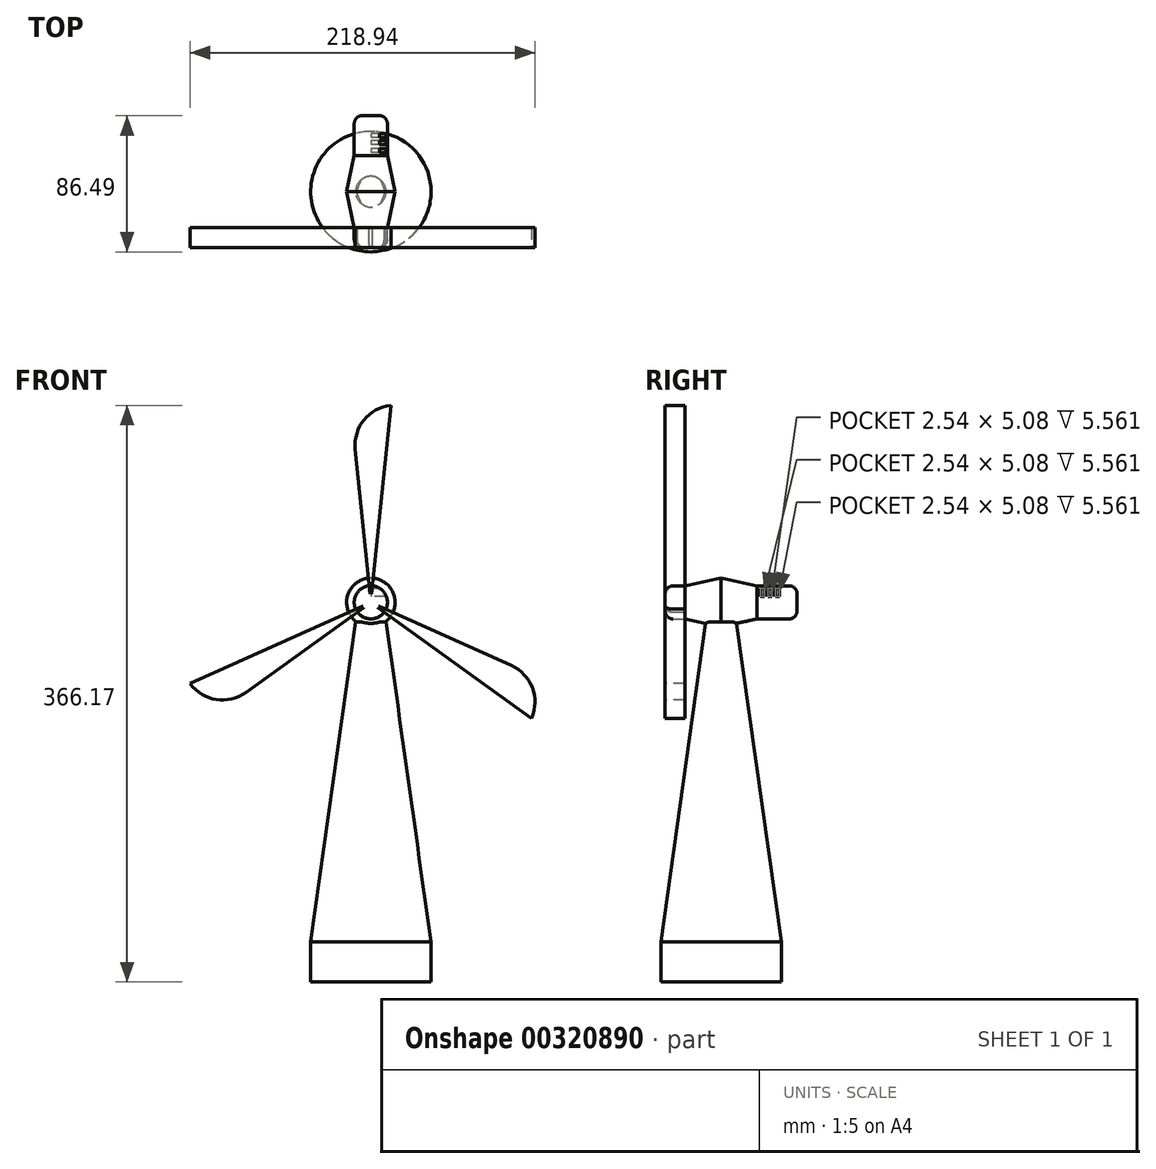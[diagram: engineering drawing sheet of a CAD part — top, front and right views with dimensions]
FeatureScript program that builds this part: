
annotation { "Feature Type Name" : "Feature", "Feature Type Description" : "" }
export const myFeature = defineFeature(function(context is Context, id is Id, definition is map)
    precondition{}
    {
        {
            var Q0;
            Q0=qCreatedBy(makeId("Top.planeOp"),FACE);
            var sketch = newSketch(context, id + "F0", { "sketchPlane" : qUnion([Q0])});
            skCircle(sketch, "E0", {"center": v(0, 0) * mm, "radius": 38.23 * mm});
            skSolve(sketch);
        }
        {
            var Q0;
            Q0=makeQuery(id+"F0.imprint","IMPRINT",FACE,{"disambiguationData":[TD([[makeQuery(id+"F0.imprint","IMPRINT",EDGE,{"derivedFrom":sQuery(id+"F0.wireOp",EDGE,"E0")}),1.0]])]});
            extrude(context, id + "F1", {"entities" : qUnion([Q0]), "depth" : 203.2 * mm, "hasDraft" : true, "draftAngle" : 8 * degree, "draftPullDirection" : true, "hasSecondDirection" : true, "secondDirectionOppositeDirection" : true, "secondDirectionDepth" : 25.4 * mm});
        }
        {
            var Q0;
            Q0=qCreatedBy(makeId("Front.planeOp"),FACE);
            var sketch = newSketch(context, id + "F2", { "sketchPlane" : qUnion([Q0])});
            skCircle(sketch, "E1", {"center": v(0, 215.62) * mm, "radius": 15.4 * mm});
            skSolve(sketch);
        }
        {
            var Q0;
            Q0=makeQuery(id+"F2.imprint","IMPRINT",FACE,{"disambiguationData":[TD([[makeQuery(id+"F2.imprint","IMPRINT",EDGE,{"derivedFrom":sQuery(id+"F2.wireOp",EDGE,"E1")}),1.0]])]});
            extrude(context, id + "F3", {"entities" : qUnion([Q0]), "operationType" : NewBodyOperationType.ADD, "depth" : 45.72 * mm, "hasDraft" : true, "draftAngle" : 12 * degree, "draftPullDirection" : true, "symmetric" : true});
        }
        {
            var Q0;
            Q0=makeQuery(id+"F3.opExtrude","CAP_FACE",FACE,{"disambiguationData":[OSD([sQuery(id+"F2.wireOp",EDGE,"E1")])],"isStart":false});
            var sketch = newSketch(context, id + "F4", { "sketchPlane" : qUnion([Q0])});
            skCircle(sketch, "E2", {"center": v(0, 215.62) * mm, "radius": 10.58 * mm});
            skSolve(sketch);
        }
        {
            var Q0;
            Q0=makeQuery(id+"F4.imprint","IMPRINT",FACE,{"disambiguationData":[TD([[makeQuery(id+"F4.imprint","IMPRINT",EDGE,{"derivedFrom":makeQuery(id+"F3.opExtrude","CAP_EDGE",EDGE,{"disambiguationData":[OSD([sQuery(id+"F2.wireOp",EDGE,"E1")])],"isStart":false})}),1.0]])]});
            extrude(context, id + "F5", {"entities" : qUnion([Q0]), "operationType" : NewBodyOperationType.ADD, "depth" : 6.35 * mm});
        }
        {
            var Q0;
            Q0=makeQuery(id+"F5.opExtrude","CAP_FACE",FACE,{"disambiguationData":[OSD([sQuery(id+"F2.wireOp",EDGE,"E1")])],"isStart":false});
            extrude(context, id + "F6", {"entities" : qUnion([Q0]), "operationType" : NewBodyOperationType.ADD, "depth" : 6.35 * mm});
        }
        {
            var Q0;
            Q0=makeQuery(id+"F6.opExtrude","CAP_FACE",FACE,{"disambiguationData":[OSD([sQuery(id+"F2.wireOp",EDGE,"E1")])],"isStart":false});
            fillet(context, id + "F7", {"entities" : qUnion([Q0]), "radius" : 5.08 * mm, "tangentPropagation" : true, "allowEdgeOverflow" : false});
        }
        {
            var Q0;
            Q0=makeQuery(id+"F6.opExtrude","CAP_FACE",FACE,{"disambiguationData":[OSD([sQuery(id+"F2.wireOp",EDGE,"E1")])],"isStart":false});
            var sketch = newSketch(context, id + "F8", { "sketchPlane" : qUnion([Q0])});
            skLineSegment(sketch, "E3", {"start": v(0, 340.77) * mm, "end": v(-12.7, 340.77) * mm});
            skLineSegment(sketch, "E4", {"start": v(0, 340.77) * mm, "end": v(12.7, 340.77) * mm});
            skLineSegment(sketch, "E5", {"start": v(-12.7, 340.77) * mm, "end": v(0, 215.62) * mm});
            skLineSegment(sketch, "E6", {"start": v(12.7, 340.77) * mm, "end": v(0, 215.62) * mm});
            skLineSegment(sketch, "E7.1.0", {"start": v(-108.38, 153.05) * mm, "end": v(-102.03, 142.05) * mm});
            skLineSegment(sketch, "E7.1.1", {"start": v(-108.38, 153.05) * mm, "end": v(-114.73, 164.05) * mm});
            skLineSegment(sketch, "E7.1.2", {"start": v(-102.03, 142.05) * mm, "end": v(0, 215.62) * mm});
            skLineSegment(sketch, "E7.1.3", {"start": v(-114.73, 164.05) * mm, "end": v(0, 215.62) * mm});
            skLineSegment(sketch, "E7.2.0", {"start": v(108.38, 153.05) * mm, "end": v(114.73, 164.05) * mm});
            skLineSegment(sketch, "E7.2.1", {"start": v(108.38, 153.05) * mm, "end": v(102.03, 142.05) * mm});
            skLineSegment(sketch, "E7.2.2", {"start": v(114.73, 164.05) * mm, "end": v(0, 215.62) * mm});
            skLineSegment(sketch, "E7.2.3", {"start": v(102.03, 142.05) * mm, "end": v(0, 215.62) * mm});
            skPoint(sketch, "E7.center", {"position": v(0, 215.62) * mm});
            skSolve(sketch);
        }
        {
            var Q0;
            {var subQ6=sQuery(id+"F8.wireOp",EDGE,"E3");Q0=makeQuery(id+"F8.imprint","IMPRINT",FACE,{"disambiguationData":[TD([[makeQuery(id+"F8.imprint","IMPRINT",EDGE,{"derivedFrom":subQ6}),1.0]])]});}
            var Q1;
            {var subQ6=sQuery(id+"F8.wireOp",EDGE,"E7.1.0");Q1=makeQuery(id+"F8.imprint","IMPRINT",FACE,{"disambiguationData":[TD([[makeQuery(id+"F8.imprint","IMPRINT",EDGE,{"derivedFrom":subQ6}),1.0]])]});}
            var Q2;
            {var subQ6=sQuery(id+"F8.wireOp",EDGE,"E7.2.0");Q2=makeQuery(id+"F8.imprint","IMPRINT",FACE,{"disambiguationData":[TD([[makeQuery(id+"F8.imprint","IMPRINT",EDGE,{"derivedFrom":subQ6}),1.0]])]});}
            extrude(context, id + "F9", {"entities" : qUnion([Q0, Q1, Q2]), "operationType" : NewBodyOperationType.ADD, "oppositeDirection" : true, "depth" : 12.7 * mm});
        }
        {
            var Q0;
            Q0=makeQuery(id+"F9.opExtrude","SWEPT_EDGE",EDGE,{"disambiguationData":[OSD([sQuery(id+"F8.wireOp",EDGE,"E3"),sQuery(id+"F8.wireOp",EDGE,"E5")])]});
            var Q1;
            Q1=makeQuery(id+"F9.opExtrude","SWEPT_EDGE",EDGE,{"disambiguationData":[OSD([sQuery(id+"F8.wireOp",EDGE,"E7.1.0"),sQuery(id+"F8.wireOp",EDGE,"E7.1.2")])]});
            var Q2;
            Q2=makeQuery(id+"F9.opExtrude","SWEPT_EDGE",EDGE,{"disambiguationData":[OSD([sQuery(id+"F8.wireOp",EDGE,"E7.2.0"),sQuery(id+"F8.wireOp",EDGE,"E7.2.2")])]});
            fillet(context, id + "F10", {"entities" : qUnion([Q0, Q1, Q2]), "radius" : 25.4 * mm, "tangentPropagation" : true, "allowEdgeOverflow" : false});
        }
        {
            var Q0;
            Q0=makeQuery(id+"F3.opExtrude","CAP_FACE",FACE,{"disambiguationData":[OSD([sQuery(id+"F2.wireOp",EDGE,"E1")])],"isStart":true});
            extrude(context, id + "F11", {"entities" : qUnion([Q0]), "operationType" : NewBodyOperationType.ADD, "depth" : 25.4 * mm});
        }
        {
            var Q0;
            Q0=makeQuery(id+"F11.opExtrude","CAP_EDGE",EDGE,{"disambiguationData":[OSD([sQuery(id+"F2.wireOp",EDGE,"E1")])],"isStart":false});
            fillet(context, id + "F12", {"entities" : qUnion([Q0]), "radius" : 5.08 * mm, "tangentPropagation" : true, "allowEdgeOverflow" : false});
        }
        {
            var Q0;
            Q0=qCreatedBy(makeId("Right.planeOp"),FACE);
            var sketch = newSketch(context, id + "F13", { "sketchPlane" : qUnion([Q0])});
            skLineSegment(sketch, "E8", {"start": v(24.88, 224.57) * mm, "end": v(24.88, 219.49) * mm});
            skLineSegment(sketch, "E9", {"start": v(24.88, 219.49) * mm, "end": v(27.42, 219.49) * mm});
            skLineSegment(sketch, "E10", {"start": v(27.42, 219.49) * mm, "end": v(27.42, 224.57) * mm});
            skLineSegment(sketch, "E11", {"start": v(27.42, 224.57) * mm, "end": v(24.88, 224.57) * mm});
            skLineSegment(sketch, "E12", {"start": v(29.9, 224.57) * mm, "end": v(29.9, 219.49) * mm});
            skLineSegment(sketch, "E13", {"start": v(29.9, 219.49) * mm, "end": v(32.45, 219.49) * mm});
            skLineSegment(sketch, "E14", {"start": v(32.45, 219.49) * mm, "end": v(32.45, 224.57) * mm});
            skLineSegment(sketch, "E15", {"start": v(32.45, 224.57) * mm, "end": v(29.9, 224.57) * mm});
            skLineSegment(sketch, "E16", {"start": v(34.49, 224.57) * mm, "end": v(34.49, 219.49) * mm});
            skLineSegment(sketch, "E17", {"start": v(34.49, 219.49) * mm, "end": v(37.03, 219.49) * mm});
            skLineSegment(sketch, "E18", {"start": v(37.03, 219.49) * mm, "end": v(37.03, 224.57) * mm});
            skLineSegment(sketch, "E19", {"start": v(37.03, 224.57) * mm, "end": v(34.49, 224.57) * mm});
            skSolve(sketch);
        }
        {
            var Q0;
            Q0=makeQuery(id+"F13.imprint","IMPRINT",FACE,{"disambiguationData":[TD([[makeQuery(id+"F13.imprint","IMPRINT",EDGE,{"derivedFrom":sQuery(id+"F13.wireOp",EDGE,"E12")}),1.0]])]});
            var Q1;
            Q1=makeQuery(id+"F13.imprint","IMPRINT",FACE,{"disambiguationData":[TD([[makeQuery(id+"F13.imprint","IMPRINT",EDGE,{"derivedFrom":sQuery(id+"F13.wireOp",EDGE,"E8")}),1.0]])]});
            var Q2;
            Q2=makeQuery(id+"F13.imprint","IMPRINT",FACE,{"disambiguationData":[TD([[makeQuery(id+"F13.imprint","IMPRINT",EDGE,{"derivedFrom":sQuery(id+"F13.wireOp",EDGE,"E16")}),1.0]])]});
            extrude(context, id + "F14", {"entities" : qUnion([Q0, Q1, Q2]), "operationType" : NewBodyOperationType.REMOVE, "depth" : 25.4 * mm});
        }
    });
